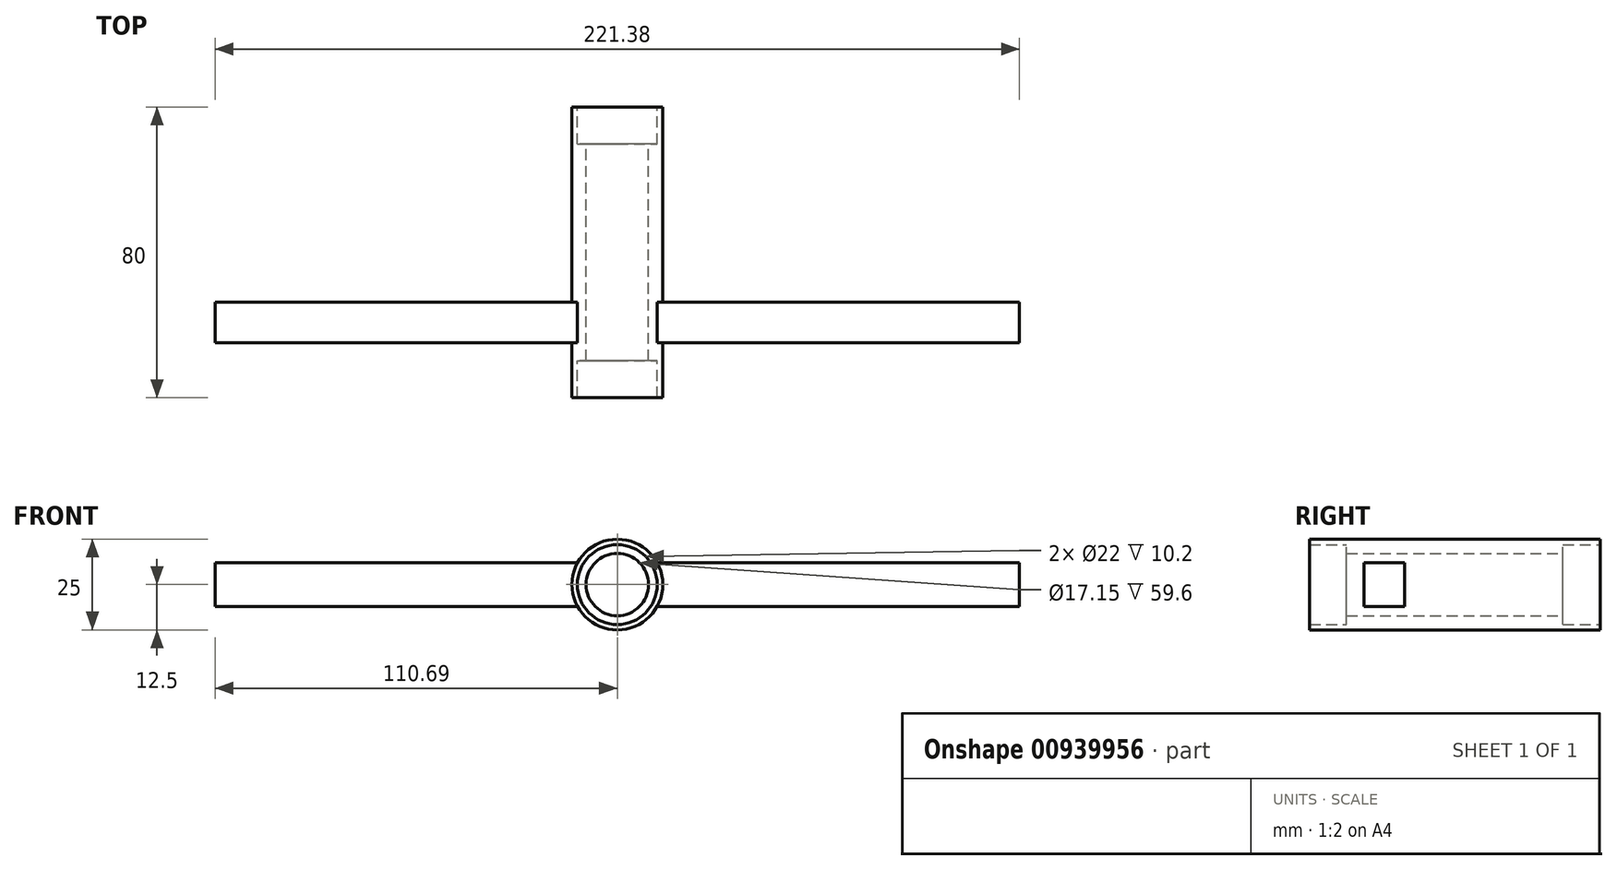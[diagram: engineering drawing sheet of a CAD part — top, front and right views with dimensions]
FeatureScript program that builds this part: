
annotation { "Feature Type Name" : "Feature", "Feature Type Description" : "" }
export const myFeature = defineFeature(function(context is Context, id is Id, definition is map)
    precondition{}
    {
        {
            var Q0;
            Q0=qCreatedBy(makeId("Front.planeOp"),FACE);
            var sketch = newSketch(context, id + "F0", { "sketchPlane" : qUnion([Q0])});
            skCircle(sketch, "E0", {"center": v(0, 0) * mm, "radius": 11 * mm});
            skCircle(sketch, "E1", {"center": v(0, 0) * mm, "radius": 12.5 * mm});
            skSolve(sketch);
        }
        {
            var Q0;
            Q0 = qSketchRegion(id + "F0", true);
            extrude(context, id + "F1", {"entities" : qUnion([Q0]), "endBound" : BoundingType.SYMMETRIC, "depth" : 80 * mm, "offsetDistance" : 25 * mm});
        }
        {
            var Q0;
            Q0=qCreatedBy(makeId("Front.planeOp"),FACE);
            var sketch = newSketch(context, id + "F2", { "sketchPlane" : qUnion([Q0])});
            skLineSegment(sketch, "E2", {"start": v(-26.45, 0) * mm, "end": v(32.7, 0) * mm, "construction": true});
            skLineSegment(sketch, "E3", {"start": v(0, 28.56) * mm, "end": v(0, -20.66) * mm, "construction": true});
            skCircle(sketch, "E4", {"center": v(0, 0) * mm, "radius": 8.57 * mm});
            skCircle(sketch, "E5.0", {"center": v(0, 0) * mm, "radius": 11 * mm});
            skSolve(sketch);
        }
        {
            var Q0;
            Q0 = qSketchRegion(id + "F2", true);
            extrude(context, id + "F3", {"entities" : qUnion([Q0]), "operationType" : NewBodyOperationType.ADD, "endBound" : BoundingType.SYMMETRIC, "depth" : 59.6 * mm, "offsetDistance" : 25 * mm});
        }
        {
            var Q0;
            Q0=qCreatedBy(makeId("Top.planeOp"),FACE);
            var sketch = newSketch(context, id + "F4", { "sketchPlane" : qUnion([Q0])});
            skLineSegment(sketch, "E6.bottom", {"start": v(-10.69, -13.78) * mm, "end": v(-110.69, -13.78) * mm});
            skLineSegment(sketch, "E6.top", {"start": v(-10.69, -24.94) * mm, "end": v(-110.69, -24.94) * mm});
            skLineSegment(sketch, "E6.left", {"start": v(-10.69, -13.78) * mm, "end": v(-10.69, -24.94) * mm});
            skLineSegment(sketch, "E6.right", {"start": v(-110.69, -13.78) * mm, "end": v(-110.69, -24.94) * mm});
            skLineSegment(sketch, "E7", {"start": v(0, 49.82) * mm, "end": v(0, -57.37) * mm, "construction": true});
            skLineSegment(sketch, "E8.MirrorCS", {"start": v(10.69, -13.78) * mm, "end": v(110.69, -13.78) * mm});
            skLineSegment(sketch, "E9.MirrorCS", {"start": v(10.69, -13.78) * mm, "end": v(10.69, -24.94) * mm});
            skLineSegment(sketch, "E10.MirrorCS", {"start": v(10.69, -24.94) * mm, "end": v(110.69, -24.94) * mm});
            skLineSegment(sketch, "E11.MirrorCS", {"start": v(110.69, -13.78) * mm, "end": v(110.69, -24.94) * mm});
            skSolve(sketch);
        }
        {
            var Q0;
            Q0 = qSketchRegion(id + "F4", true);
            extrude(context, id + "F5", {"entities" : qUnion([Q0]), "operationType" : NewBodyOperationType.ADD, "endBound" : BoundingType.SYMMETRIC, "depth" : 12 * mm, "offsetDistance" : 25 * mm});
        }
    });
